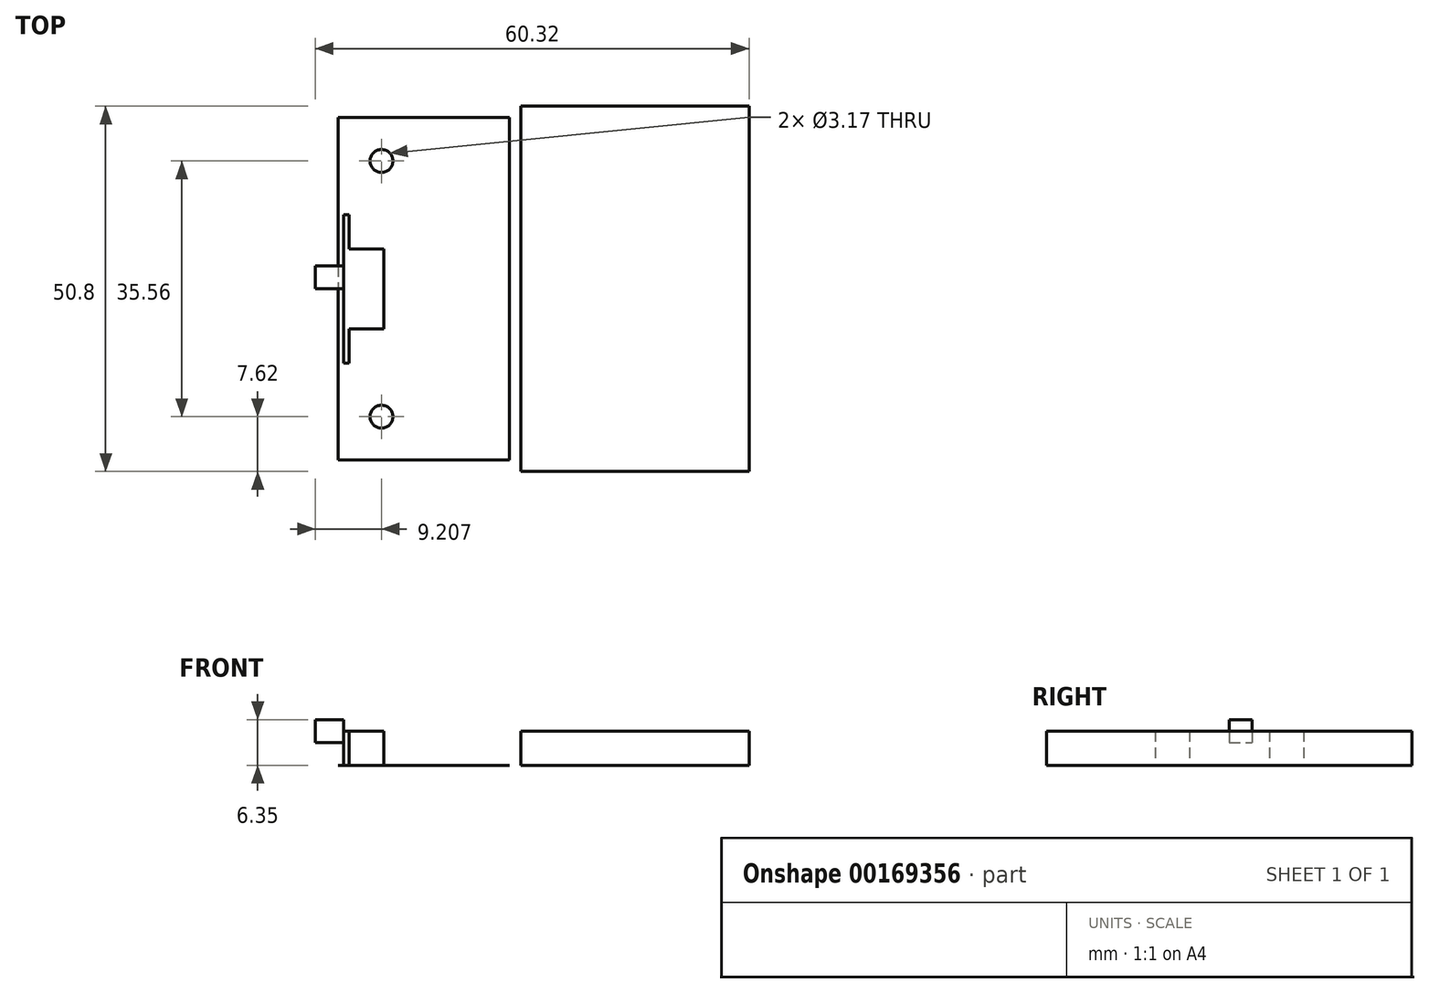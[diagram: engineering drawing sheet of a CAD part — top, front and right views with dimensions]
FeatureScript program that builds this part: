
annotation { "Feature Type Name" : "Feature", "Feature Type Description" : "" }
export const myFeature = defineFeature(function(context is Context, id is Id, definition is map)
    precondition{}
    {
        {
            var Q0;
            Q0=qCreatedBy(makeId("Top.planeOp"),FACE);
            var sketch = newSketch(context, id + "F0", { "sketchPlane" : qUnion([Q0])});
            skLineSegment(sketch, "E0.bottom", {"start": v(-3.17, 25.4) * mm, "end": v(28.58, 25.4) * mm});
            skLineSegment(sketch, "E0.top", {"start": v(-3.17, -25.4) * mm, "end": v(28.58, -25.4) * mm});
            skLineSegment(sketch, "E0.left", {"start": v(-3.17, 25.4) * mm, "end": v(-3.17, -25.4) * mm});
            skLineSegment(sketch, "E0.right", {"start": v(28.58, 25.4) * mm, "end": v(28.58, -25.4) * mm});
            skPoint(sketch, "E0.middle", {"position": v(12.7, 0) * mm});
            skSolve(sketch);
        }
        {
            var Q0;
            Q0=makeQuery(id+"F0.imprint","IMPRINT",FACE,{"disambiguationData":[TD([[makeQuery(id+"F0.imprint","IMPRINT",EDGE,{"derivedFrom":sQuery(id+"F0.wireOp",EDGE,"E0.bottom")}),-1.0]])]});
            extrude(context, id + "F1", {"entities" : qUnion([Q0]), "depth" : 4.76 * mm});
        }
        {
            var Q0;
            Q0=qCreatedBy(makeId("Top.planeOp"),FACE);
            var sketch = newSketch(context, id + "F2", { "sketchPlane" : qUnion([Q0])});
            skLineSegment(sketch, "E1.bottom", {"start": v(-4.76, 23.81) * mm, "end": v(-28.57, 23.81) * mm});
            skLineSegment(sketch, "E1.top", {"start": v(-4.76, -23.81) * mm, "end": v(-28.57, -23.81) * mm});
            skLineSegment(sketch, "E1.left", {"start": v(-4.76, 23.81) * mm, "end": v(-4.76, -23.81) * mm});
            skLineSegment(sketch, "E1.right", {"start": v(-28.57, 23.81) * mm, "end": v(-28.57, -23.81) * mm});
            skPoint(sketch, "E1.middle", {"position": v(-16.67, 0) * mm});
            skCircle(sketch, "E2", {"center": v(-22.54, 17.78) * mm, "radius": 1.59 * mm});
            skLineSegment(sketch, "E3", {"start": v(-28.57, 0) * mm, "end": v(-4.76, 0) * mm, "construction": true});
            skCircle(sketch, "E4.MirrorC", {"center": v(-22.54, -17.78) * mm, "radius": 1.59 * mm});
            skSolve(sketch);
        }
        {
            var Q0;
            Q0=qSketchRegion(id+"F2",true);
            extrude(context, id + "F3", {"entities" : qUnion([Q0]), "depth" : 3 / 812.8 * mm});
        }
        {
            var Q0;
            Q0=makeQuery(id+"F3.opExtrude","CAP_FACE",FACE,{"disambiguationData":[OSD([sQuery(id+"F2.wireOp",EDGE,"E1.bottom"),sQuery(id+"F2.wireOp",EDGE,"E1.top"),sQuery(id+"F2.wireOp",EDGE,"E1.left"),sQuery(id+"F2.wireOp",EDGE,"E1.right"),sQuery(id+"F2.wireOp",EDGE,"E2"),sQuery(id+"F2.wireOp",EDGE,"E4.MirrorC")])],"isStart":false});
            var sketch = newSketch(context, id + "F4", { "sketchPlane" : qUnion([Q0])});
            skLineSegment(sketch, "E5", {"start": v(-27.78, 10.32) * mm, "end": v(-27.78, -10.32) * mm});
            skLineSegment(sketch, "E6", {"start": v(-27.78, -10.32) * mm, "end": v(-27.02, -10.32) * mm});
            skLineSegment(sketch, "E7", {"start": v(-27.02, -10.32) * mm, "end": v(-27.02, -5.56) * mm});
            skLineSegment(sketch, "E8", {"start": v(-27.02, -5.56) * mm, "end": v(-22.23, -5.56) * mm});
            skLineSegment(sketch, "E9", {"start": v(-22.23, -5.56) * mm, "end": v(-22.23, 5.56) * mm});
            skLineSegment(sketch, "E10", {"start": v(-22.23, 5.56) * mm, "end": v(-27.02, 5.56) * mm});
            skLineSegment(sketch, "E11", {"start": v(-27.02, 5.56) * mm, "end": v(-27.02, 10.32) * mm});
            skLineSegment(sketch, "E12", {"start": v(-27.02, 10.32) * mm, "end": v(-27.78, 10.32) * mm});
            skLineSegment(sketch, "E13", {"start": v(-27.78, 0) * mm, "end": v(-18.34, 0) * mm, "construction": true});
            skSolve(sketch);
        }
        {
            var Q0;
            Q0=qSketchRegion(id+"F4",true);
            extrude(context, id + "F5", {"entities" : qUnion([Q0]), "depth" : 4.76 * mm});
        }
        {
            var Q0;
            Q0=makeQuery(id+"F5.opExtrude","SWEPT_FACE",FACE,{"disambiguationData":[OSD([sQuery(id+"F4.wireOp",EDGE,"E5")])]});
            var sketch = newSketch(context, id + "F6", { "sketchPlane" : qUnion([Q0])});
            skLineSegment(sketch, "E14", {"start": v(-10.32, 4.76) * mm, "end": v(10.32, 4.76) * mm, "construction": true});
            skLineSegment(sketch, "E15.bottom", {"start": v(0, 6.35) * mm, "end": v(-3.18, 6.35) * mm});
            skLineSegment(sketch, "E15.top", {"start": v(0, 3.18) * mm, "end": v(-3.17, 3.17) * mm});
            skLineSegment(sketch, "E15.left", {"start": v(0, 6.35) * mm, "end": v(0, 3.17) * mm});
            skLineSegment(sketch, "E15.right", {"start": v(-3.18, 6.35) * mm, "end": v(-3.17, 3.17) * mm});
            skPoint(sketch, "E15.middle", {"position": v(-1.59, 4.76) * mm});
            skSolve(sketch);
        }
        {
            var Q0;
            Q0=qSketchRegion(id+"F6",true);
            extrude(context, id + "F7", {"entities" : qUnion([Q0]), "operationType" : NewBodyOperationType.ADD, "depth" : 3.97 * mm});
        }
    });
